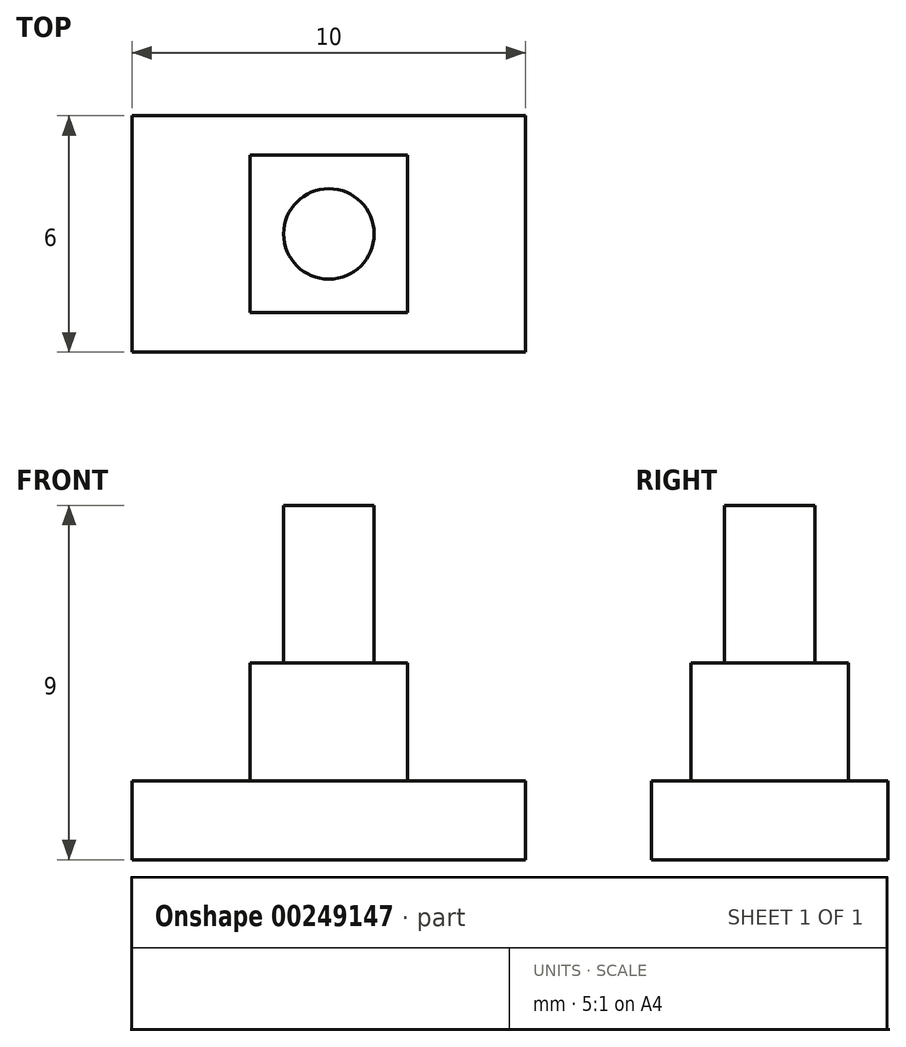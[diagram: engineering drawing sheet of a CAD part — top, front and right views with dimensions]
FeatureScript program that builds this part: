
annotation { "Feature Type Name" : "Feature", "Feature Type Description" : "" }
export const myFeature = defineFeature(function(context is Context, id is Id, definition is map)
    precondition{}
    {
        {
            var Q0;
            Q0=qCreatedBy(makeId("Top.planeOp"),FACE);
            var sketch = newSketch(context, id + "F0", { "sketchPlane" : qUnion([Q0])});
            skLineSegment(sketch, "E0.bottom", {"start": v(2, -2) * mm, "end": v(-2, -2) * mm});
            skLineSegment(sketch, "E0.top", {"start": v(2, 2) * mm, "end": v(-2, 2) * mm});
            skLineSegment(sketch, "E0.left", {"start": v(2, -2) * mm, "end": v(2, 2) * mm});
            skLineSegment(sketch, "E0.right", {"start": v(-2, -2) * mm, "end": v(-2, 2) * mm});
            skPoint(sketch, "E0.middle", {"position": v(0, 0) * mm});
            skCircle(sketch, "E1", {"center": v(0, 0) * mm, "radius": 1.15 * mm});
            skSolve(sketch);
        }
        {
            var Q0;
            Q0=makeQuery(id+"F0.imprint","IMPRINT",FACE,{"disambiguationData":[TD([[makeQuery(id+"F0.imprint","IMPRINT",EDGE,{"derivedFrom":sQuery(id+"F0.wireOp",EDGE,"E1")}),1.0]])]});
            var Q1;
            Q1=sQuery(id+"F0.wireOp",EDGE,"E1");
            extrude(context, id + "F1", {"entities" : qUnion([Q0]), "surfaceEntities" : qUnion([Q1]), "endBound" : BoundingType.SYMMETRIC, "oppositeDirection" : true, "depth" : 8 * mm});
        }
        {
            var Q0;
            Q0=makeQuery(id+"F0.imprint","IMPRINT",FACE,{"disambiguationData":[TD([[makeQuery(id+"F0.imprint","IMPRINT",EDGE,{"derivedFrom":sQuery(id+"F0.wireOp",EDGE,"E0.bottom")}),-1.0]])]});
            var Q1;
            Q1=makeQuery(id+"F0.imprint","IMPRINT",FACE,{"disambiguationData":[TD([[makeQuery(id+"F0.imprint","IMPRINT",EDGE,{"derivedFrom":sQuery(id+"F0.wireOp",EDGE,"E1")}),1.0]])]});
            extrude(context, id + "F2", {"entities" : qUnion([Q0, Q1]), "operationType" : NewBodyOperationType.ADD, "oppositeDirection" : true, "depth" : 3.2 * mm});
        }
        {
            var Q0;
            Q0=qCreatedBy(makeId("Top.planeOp"),FACE);
            var sketch = newSketch(context, id + "F3", { "sketchPlane" : qUnion([Q0])});
            skLineSegment(sketch, "E2.bottom", {"start": v(5, -3) * mm, "end": v(-5, -3) * mm});
            skLineSegment(sketch, "E2.top", {"start": v(5, 3) * mm, "end": v(-5, 3) * mm});
            skLineSegment(sketch, "E2.left", {"start": v(5, -3) * mm, "end": v(5, 3) * mm});
            skLineSegment(sketch, "E2.right", {"start": v(-5, -3) * mm, "end": v(-5, 3) * mm});
            skPoint(sketch, "E2.middle", {"position": v(0, 0) * mm});
            skSolve(sketch);
        }
        {
            var Q0;
            Q0 = qSketchRegion(id + "F3", true);
            extrude(context, id + "F4", {"entities" : qUnion([Q0]), "operationType" : NewBodyOperationType.ADD, "oppositeDirection" : true, "depth" : 5 * mm, "hasSecondDirection" : true, "secondDirectionOppositeDirection" : true, "secondDirectionDepth" : 3 * mm});
        }
    });
